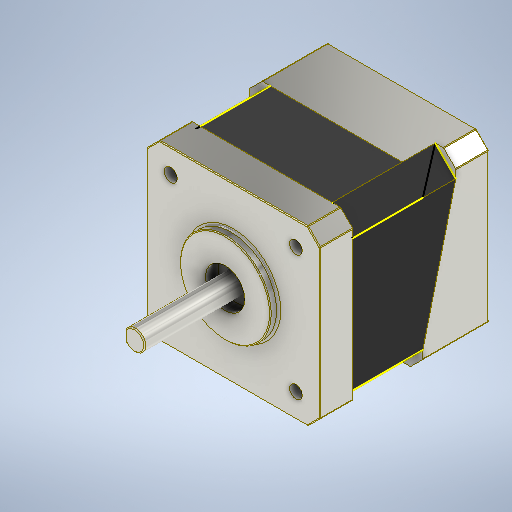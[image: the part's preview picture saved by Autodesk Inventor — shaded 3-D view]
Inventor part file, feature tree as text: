
AUTODESK INVENTOR PART (.ipt)
format: ipt  version: 2025 (Build 290162000, 162)  size: 621,568 bytes
history: native  units: mm
features: extrude x18, chamfer x12, fillet x6, sketch x5, thread x4
ambient origin geometry x8: Origin, YZ Plane, XZ Plane, XY Plane, X Axis, Y Axis, Z Axis, Center Point
bodies: Solid1 (feature_tree)
feature tree (45):
  extrude  "Extrusion1"  Depth=41.0mm
  chamfer  "Chamfer6"  Distance=41.0mm
  chamfer  "Chamfer7"  Distance=2.0mm Angle=45.0deg
  chamfer  "Chamfer8"  Distance=2.0mm Angle=45.0deg
  chamfer  "Chamfer9"  Distance=2.0mm Angle=45.0deg
  chamfer  "Chamfer10"  Distance=16.0mm
  chamfer  "Chamfer11"  Distance=2.0mm Angle=45.0deg
  chamfer  "Chamfer12"  Distance=2.0mm Angle=45.0deg
  chamfer  "Chamfer13"  Distance=16.0mm
  chamfer  "Chamfer14"  Distance=2.0mm Angle=45.0deg
  chamfer  "Chamfer15"  Distance=0.011mm
  chamfer  "Chamfer16"  Distance=2.0mm Angle=45.0deg
  chamfer  "Chamfer17"  Distance=2.0mm Angle=45.0deg
  extrude  "Extrusion3"  Depth=2.0mm TaperAngle=45.0deg
  extrude  "Extrusion4"  Depth=0.3mm TaperAngle=0.0deg
  extrude  "Extrusion5"  Depth=0.3mm TaperAngle=0.0deg
  extrude  "Extrusion6"  Depth=0.3mm TaperAngle=0.0deg
  extrude  "Extrusion7"  Depth=0.3mm TaperAngle=0.0deg
  extrude  "Extrusion8"  Depth=0.3mm TaperAngle=0.0deg
  extrude  "Extrusion9"  Depth=0.3mm
  extrude  "Extrusion10"  Depth=2.0mm TaperAngle=0.0deg
  extrude  "Extrusion11"  Depth=0.3mm
  fillet  "Fillet1"  Radius=3.0mm
  extrude  "Extrusion12"  Depth=0.3mm
  thread  "Thread1"  [1 undecoded]
  thread  "Thread2"  [1 undecoded]
  thread  "Thread3"  [1 undecoded]
  thread  "Thread4"  [1 undecoded]
  extrude  "Extrusion13"  Depth=0.25mm
  extrude  "Extrusion14"  Depth=0.3mm
  extrude  "Extrusion15"  Depth=0.3mm
  fillet  "Fillet2"  Radius=3.2mm
  fillet  "Fillet3"  Radius=5.8mm
  extrude  "Extrusion16"  Depth=0.3mm
  extrude  "Extrusion17"  Depth=0.3mm
  extrude  "Extrusion18"  Depth=0.3mm
  extrude  "Extrusion19"  Depth=0.3mm
  fillet  "Fillet4"  Radius=3.1mm
  fillet  "Fillet5"  Radius=5.8mm
  fillet  "Fillet6"  Radius=5.8mm
  sketch  "Sketch10"  dims[d0=42.0mm d1=42.0mm d2=41.0mm d3=0.0mm]
  sketch  "Sketch23"  dims[d32=5.0mm d33=2.0mm d34=45.0deg d35=8.0mm d36=25.0mm d37=8.0mm d38=3.0mm d39=2.0mm d40=45.0deg d41=3.0mm d42=2.0mm d43=45.0deg d44=3.0mm d45=2.0mm d46=45.0deg d47=0.0mm d48=16.0mm d49=25.0mm]
  sketch  "Sketch27"  dims[d50=5.0mm d51=2.0mm d52=45.0deg d53=0.002mm d54=16.998mm d55=8.0mm d56=3.0mm d57=2.0mm d58=45.0deg d59=3.0mm d60=2.0mm d61=45.0deg d62=0.0mm d63=16.0mm d64=25.0mm d65=5.0mm d66=2.0mm d67=45.0deg d68=0.011mm d69=16.989mm d70=8.0mm d71=3.0mm d72=2.0mm d73=45.0deg d74=3.0mm d75=2.0mm d76=45.0deg]
  sketch  "Sketch32"  dims[d77=0.0mm d78=16.0mm d79=25.0mm]
  sketch  "Sketch35"  dims[d80=5.0mm d81=2.0mm d82=45.0deg d83=0.015mm d84=16.985mm d85=8.0mm d86=3.0mm d87=2.0mm d88=45.0deg d89=17.0mm d90=0.0mm d91=0.01mm d92=0.0mm d93=0.01mm d94=0.0mm d95=0.01mm d96=0.0mm d97=0.01mm d98=0.0mm d99=22.0mm d100=2.0mm d101=0.0mm d102=9.5mm d103=3.0mm d104=0.0mm d105=5.0mm d106=25.0mm d107=0.0mm d108=15.0mm d109=4.5mm d110=25.0mm d111=0.0mm d112=0.25mm d113=5.8mm d114=5.8mm d115=3.2mm d116=5.8mm d117=5.8mm d118=3.1mm d119=5.8mm d120=5.8mm d121=3.1mm d122=5.8mm d123=5.8mm d124=3.1mm d125=50.0mm d126=0.0mm d127=4.0mm d128=0.0mm d129=4.0mm d130=0.0mm d131=4.0mm d132=0.0mm d133=4.0mm d134=0.0mm d135=7.0mm d136=4.0mm d137=0.0mm d138=5.8mm d139=5.8mm d140=5.8mm d141=5.8mm d142=2.5mm d143=0.0mm d144=16.0mm d145=8.0mm d146=2.0mm d147=4.3mm d148=0.0mm d149=0.5mm d150=0.2mm d151=5.5mm d152=15.0mm d153=0.5mm d154=6.0mm d155=0.0mm d156=3.9mm d157=13.0mm d158=1.0mm d159=4.5mm d160=0.0mm d161=7.8mm d162=3.9mm d163=4.5mm d164=0.0mm d165=4.0mm d166=1.0mm d167=1.0mm d168=1.0mm d169=1.0mm d170=0.84mm d171=0.0mm d189=0.2mm d190=0.3mm d191=0.3mm]
note: 4 required parameter values undecoded (feature->parameter linkage not recoverable at this tier; creation-order binding heuristic only, values carry confidence <= 0.55)
